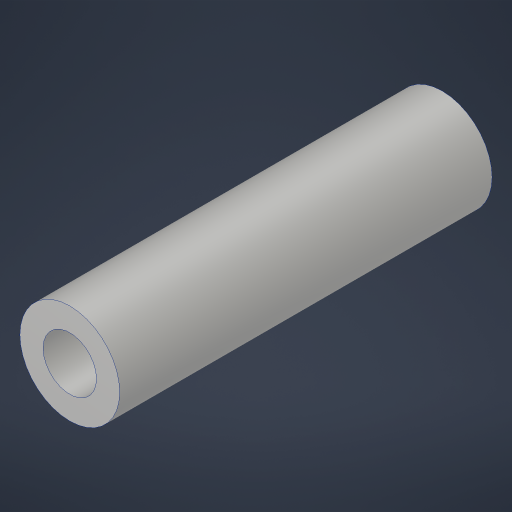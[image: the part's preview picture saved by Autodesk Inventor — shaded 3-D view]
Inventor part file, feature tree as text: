
AUTODESK INVENTOR PART (.ipt)
format: ipt  version: 2023.4 (Build 274418000, 418)  size: 176,128 bytes
history: native  units: in
note: dims shown in document units (in); Inventor stores cm internally (conversion verified against a paired STEP export)
features: extrude x1, hole x1
ambient origin geometry x8: Origin, YZ Plane, XZ Plane, XY Plane, X Axis, Y Axis, Z Axis, Center Point
bodies: Solid1 (feature_tree)
feature tree (2):
  extrude  "Extrusion1"  Depth=1.3999in
  hole  "Hole1"  [1 undecoded]
note: 1 required parameter value undecoded (feature->parameter linkage not recoverable at this tier; creation-order binding heuristic only, values carry confidence <= 0.55)
